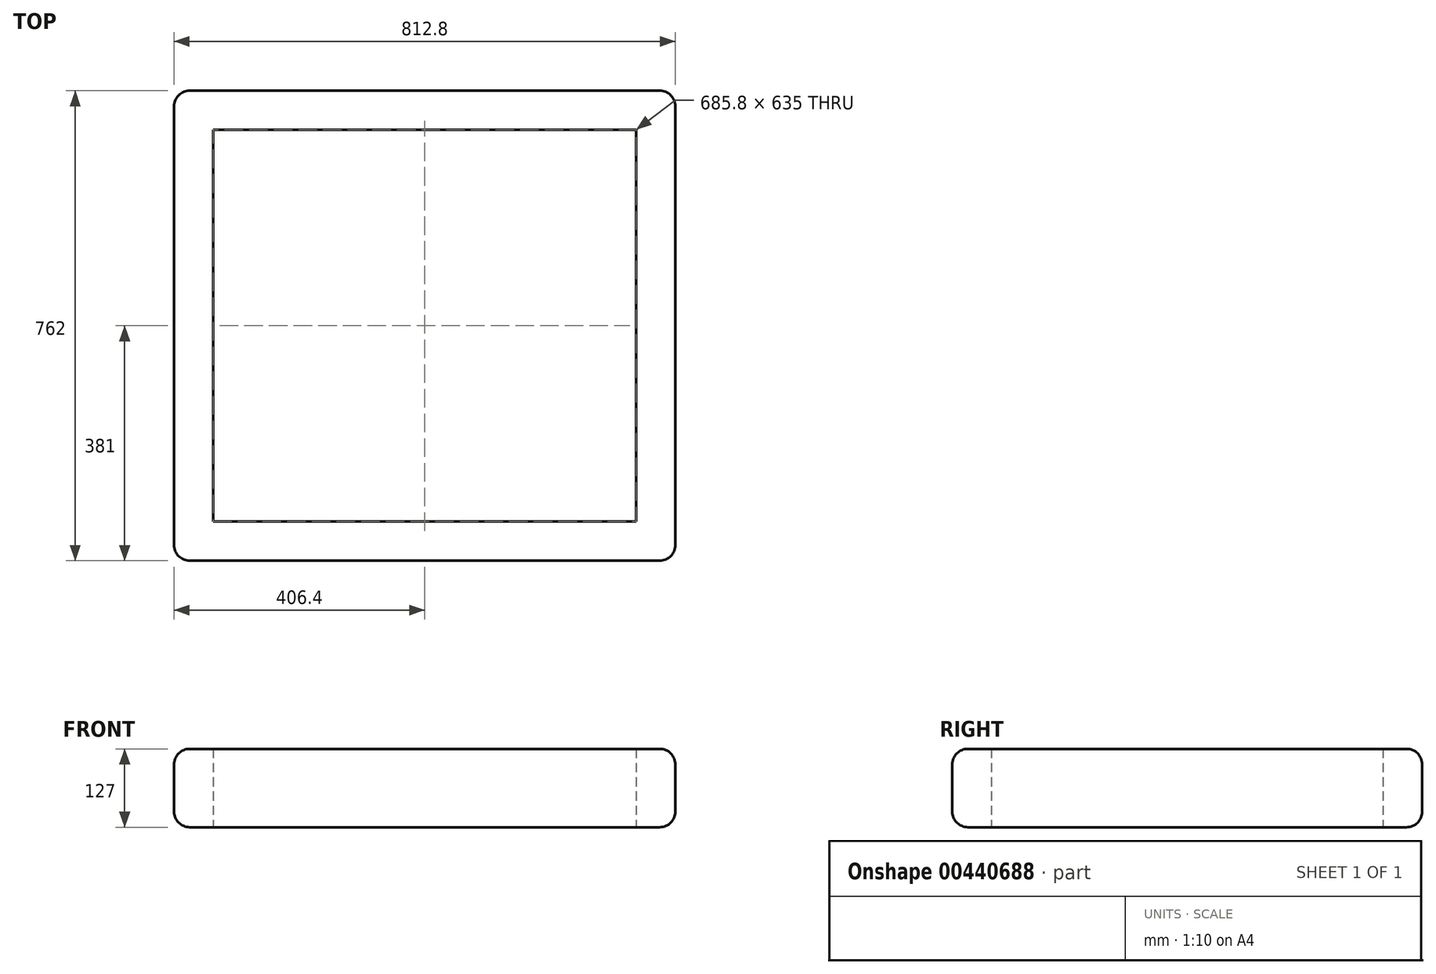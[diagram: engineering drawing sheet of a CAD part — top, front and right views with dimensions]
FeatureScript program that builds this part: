
annotation { "Feature Type Name" : "Feature", "Feature Type Description" : "" }
export const myFeature = defineFeature(function(context is Context, id is Id, definition is map)
    precondition{}
    {
        {
            var Q0;
            Q0=qCreatedBy(makeId("Top.planeOp"),FACE);
            var sketch = newSketch(context, id + "F0", { "sketchPlane" : qUnion([Q0])});
            skLineSegment(sketch, "E0.bottom", {"start": v(406.4, 381) * mm, "end": v(-406.4, 381) * mm});
            skLineSegment(sketch, "E0.top", {"start": v(406.4, -381) * mm, "end": v(-406.4, -381) * mm});
            skLineSegment(sketch, "E0.left", {"start": v(406.4, 381) * mm, "end": v(406.4, -381) * mm});
            skLineSegment(sketch, "E0.right", {"start": v(-406.4, 381) * mm, "end": v(-406.4, -381) * mm});
            skPoint(sketch, "E0.middle", {"position": v(0, 0) * mm});
            skSolve(sketch);
        }
        {
            var Q0;
            Q0=makeQuery(id+"F0.imprint","IMPRINT",FACE,{"disambiguationData":[TD([[makeQuery(id+"F0.imprint","IMPRINT",EDGE,{"derivedFrom":sQuery(id+"F0.wireOp",EDGE,"E0.bottom")}),1.0]])]});
            var sketch = newSketch(context, id + "F1", { "sketchPlane" : qUnion([Q0])});
            skLineSegment(sketch, "E1.bottom", {"start": v(342.9, 317.5) * mm, "end": v(-342.9, 317.5) * mm});
            skLineSegment(sketch, "E1.top", {"start": v(342.9, -317.5) * mm, "end": v(-342.9, -317.5) * mm});
            skLineSegment(sketch, "E1.left", {"start": v(342.9, 317.5) * mm, "end": v(342.9, -317.5) * mm});
            skLineSegment(sketch, "E1.right", {"start": v(-342.9, 317.5) * mm, "end": v(-342.9, -317.5) * mm});
            skPoint(sketch, "E1.middle", {"position": v(0, 0) * mm});
            skSolve(sketch);
        }
        {
            var Q0;
            Q0=makeQuery(id+"F0.imprint","IMPRINT",FACE,{"disambiguationData":[TD([[makeQuery(id+"F0.imprint","IMPRINT",EDGE,{"derivedFrom":sQuery(id+"F0.wireOp",EDGE,"E0.bottom")}),1.0]])]});
            extrude(context, id + "F2", {"entities" : qUnion([Q0]), "depth" : 127 * mm});
        }
        {
            var Q0;
            Q0=makeQuery(id+"F1.imprint","IMPRINT",FACE,{"disambiguationData":[TD([[makeQuery(id+"F1.imprint","IMPRINT",EDGE,{"derivedFrom":sQuery(id+"F1.wireOp",EDGE,"E1.bottom")}),1.0]])]});
            extrude(context, id + "F3", {"entities" : qUnion([Q0]), "operationType" : NewBodyOperationType.REMOVE, "depth" : 215.9 * mm});
        }
        {
            var Q0;
            Q0=makeQuery(id+"F2.opExtrude","CAP_EDGE",EDGE,{"disambiguationData":[OSD([sQuery(id+"F0.wireOp",EDGE,"E0.left")])],"isStart":false});
            var Q1;
            Q1=makeQuery(id+"F2.opExtrude","CAP_EDGE",EDGE,{"disambiguationData":[OSD([sQuery(id+"F0.wireOp",EDGE,"E0.bottom")])],"isStart":false});
            var Q2;
            Q2=makeQuery(id+"F2.opExtrude","CAP_EDGE",EDGE,{"disambiguationData":[OSD([sQuery(id+"F0.wireOp",EDGE,"E0.right")])],"isStart":false});
            var Q3;
            Q3=makeQuery(id+"F2.opExtrude","CAP_EDGE",EDGE,{"disambiguationData":[OSD([sQuery(id+"F0.wireOp",EDGE,"E0.top")])],"isStart":false});
            var Q4;
            Q4=makeQuery(id+"F2.opExtrude","CAP_EDGE",EDGE,{"disambiguationData":[OSD([sQuery(id+"F0.wireOp",EDGE,"E0.right")])],"isStart":true});
            var Q5;
            Q5=makeQuery(id+"F2.opExtrude","SWEPT_EDGE",EDGE,{"disambiguationData":[OSD([sQuery(id+"F0.wireOp",EDGE,"E0.top"),sQuery(id+"F0.wireOp",EDGE,"E0.right")])]});
            var Q6;
            Q6=makeQuery(id+"F2.opExtrude","SWEPT_EDGE",EDGE,{"disambiguationData":[OSD([sQuery(id+"F0.wireOp",EDGE,"E0.bottom"),sQuery(id+"F0.wireOp",EDGE,"E0.right")])]});
            var Q7;
            Q7=makeQuery(id+"F2.opExtrude","SWEPT_EDGE",EDGE,{"disambiguationData":[OSD([sQuery(id+"F0.wireOp",EDGE,"E0.top"),sQuery(id+"F0.wireOp",EDGE,"E0.left")])]});
            var Q8;
            Q8=makeQuery(id+"F2.opExtrude","SWEPT_FACE",FACE,{"disambiguationData":[OSD([sQuery(id+"F0.wireOp",EDGE,"E0.left")])]});
            var Q9;
            Q9=makeQuery(id+"F2.opExtrude","CAP_EDGE",EDGE,{"disambiguationData":[OSD([sQuery(id+"F0.wireOp",EDGE,"E0.bottom")])],"isStart":true});
            var Q10;
            Q10=makeQuery(id+"F2.opExtrude","CAP_EDGE",EDGE,{"disambiguationData":[OSD([sQuery(id+"F0.wireOp",EDGE,"E0.top")])],"isStart":true});
            fillet(context, id + "F4", {"entities" : qUnion([Q0, Q1, Q2, Q3, Q4, Q5, Q6, Q7, Q8, Q9, Q10]), "radius" : 25.4 * mm, "tangentPropagation" : true, "allowEdgeOverflow" : false});
        }
    });
